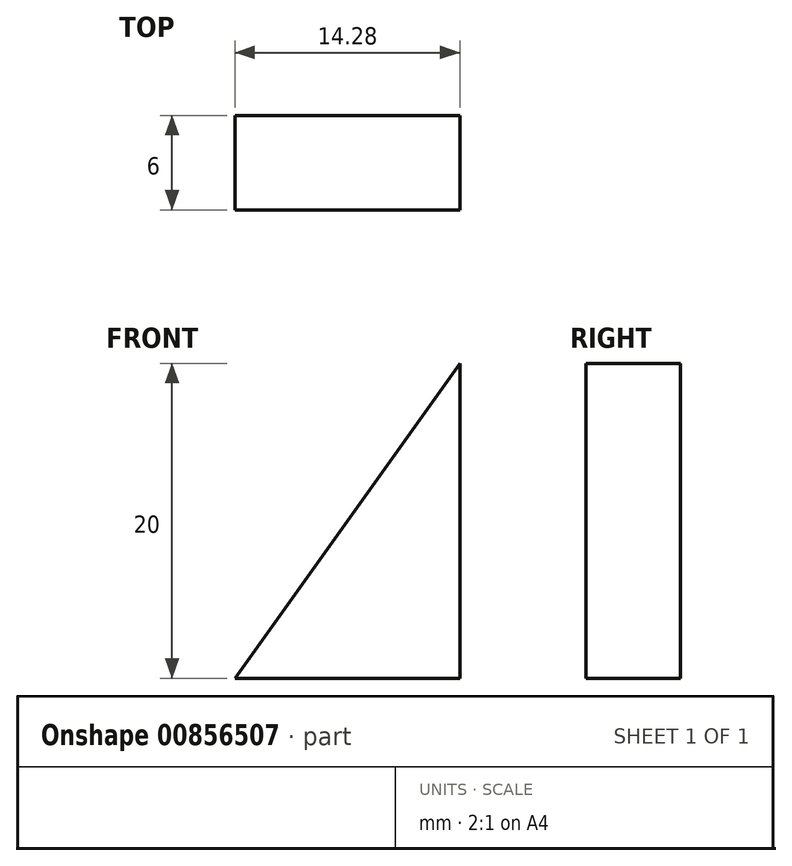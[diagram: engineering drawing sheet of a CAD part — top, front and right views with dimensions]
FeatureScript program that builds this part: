
annotation { "Feature Type Name" : "Feature", "Feature Type Description" : "" }
export const myFeature = defineFeature(function(context is Context, id is Id, definition is map)
    precondition{}
    {
        {
            var Q0;
            Q0=qCreatedBy(makeId("Top.planeOp"),FACE);
            var sketch = newSketch(context, id + "F0", { "sketchPlane" : qUnion([Q0])});
            skLineSegment(sketch, "E0.bottom", {"start": v(7.14, 3) * mm, "end": v(-7.14, 3) * mm});
            skLineSegment(sketch, "E0.top", {"start": v(7.14, -3) * mm, "end": v(-7.14, -3) * mm});
            skLineSegment(sketch, "E0.left", {"start": v(7.14, 3) * mm, "end": v(7.14, -3) * mm});
            skLineSegment(sketch, "E0.right", {"start": v(-7.14, 3) * mm, "end": v(-7.14, -3) * mm});
            skPoint(sketch, "E0.middle", {"position": v(0, 0) * mm});
            skSolve(sketch);
        }
        {
            var Q0;
            Q0=qSketchRegion(id+"F0",true);
            var Q1;
            Q1=makeQuery(id+"F0.imprint","IMPRINT",FACE,{"disambiguationData":[TD([[makeQuery(id+"F0.imprint","IMPRINT",EDGE,{"derivedFrom":sQuery(id+"F0.wireOp",EDGE,"E0.bottom")}),1.0]])]});
            extrude(context, id + "F1", {"entities" : qUnion([Q0, Q1]), "depth" : 20 * mm, "offsetDistance" : 25 * mm});
        }
        {
            var Q0;
            Q0=makeQuery(id+"F1.opExtrude","CAP_EDGE",EDGE,{"disambiguationData":[OSD([sQuery(id+"F0.wireOp",EDGE,"E0.right")])],"isStart":false});
            chamfer(context, id + "F2", {"entities" : qUnion([Q0]), "chamferType" : ChamferType.TWO_OFFSETS, "width1" : 14.28 * mm, "oppositeDirection" : false, "width2" : 20 * mm, "tangentPropagation" : true});
        }
    });
